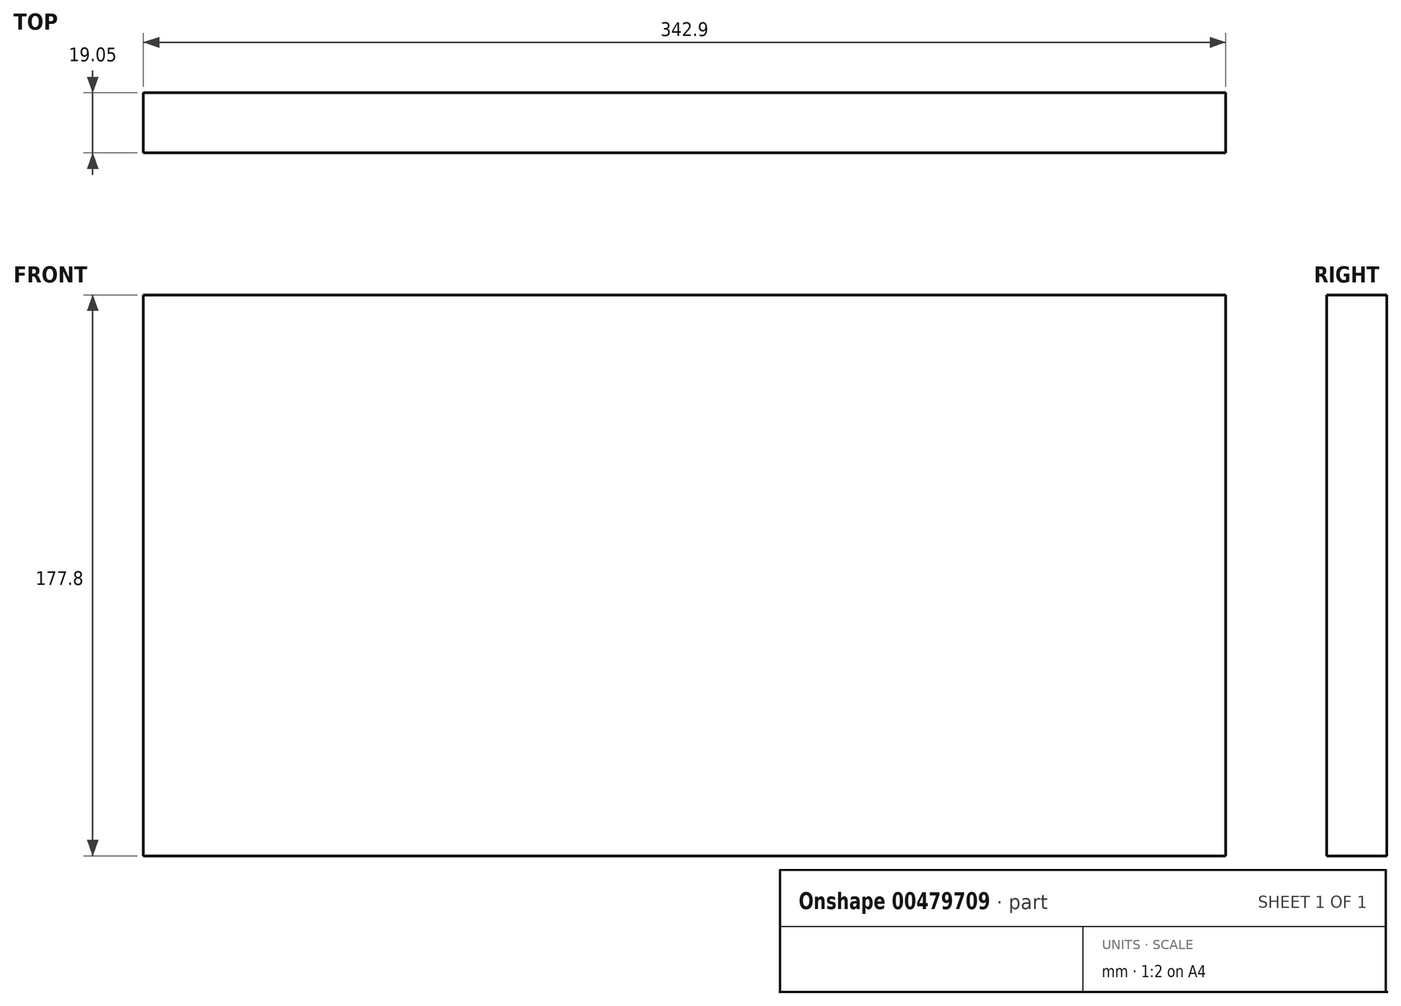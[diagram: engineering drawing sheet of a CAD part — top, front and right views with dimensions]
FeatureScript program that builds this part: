
annotation { "Feature Type Name" : "Feature", "Feature Type Description" : "" }
export const myFeature = defineFeature(function(context is Context, id is Id, definition is map)
    precondition{}
    {
        {
            var Q0;
            Q0=qCreatedBy(makeId("Front.planeOp"),FACE);
            var sketch = newSketch(context, id + "F0", { "sketchPlane" : qUnion([Q0])});
            skLineSegment(sketch, "E0.rect.bottom", {"start": v(171.45, -88.9) * mm, "end": v(-171.45, -88.9) * mm});
            skLineSegment(sketch, "E0.rect.top", {"start": v(171.45, 88.9) * mm, "end": v(-171.45, 88.9) * mm});
            skLineSegment(sketch, "E0.rect.left", {"start": v(171.45, -88.9) * mm, "end": v(171.45, 88.9) * mm});
            skLineSegment(sketch, "E0.rect.right", {"start": v(-171.45, -88.9) * mm, "end": v(-171.45, 88.9) * mm});
            skPoint(sketch, "E0.rect.middle", {"position": v(0, 0) * mm});
            skSolve(sketch);
        }
        {
            var Q0;
            Q0=qSketchRegion(id+"F0",true);
            extrude(context, id + "F1", {"entities" : qUnion([Q0]), "depth" : 19.05 * mm});
        }
    });
